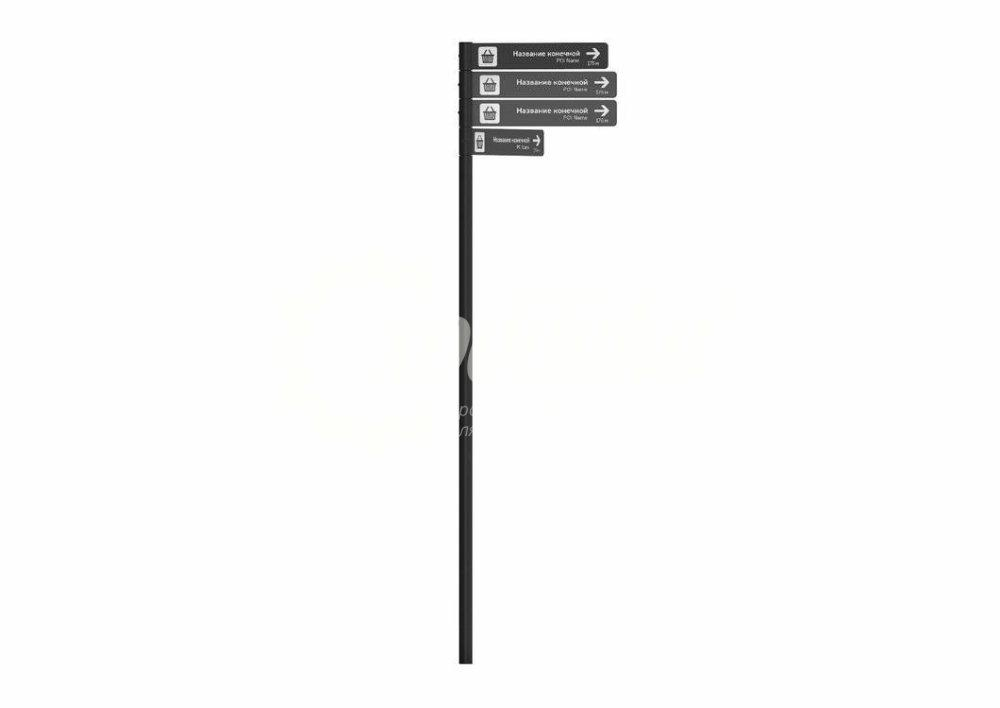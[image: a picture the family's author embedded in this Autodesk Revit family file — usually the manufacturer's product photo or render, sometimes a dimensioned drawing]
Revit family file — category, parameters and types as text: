
# Revit family: 11093 Указатель «Яуза» А 2.0 с табличками Хоббика
name_source: partatom
category: Антураж
revit_build: Autodesk Revit 2018 (Build: 20180423_1000(x64)
units: mm (PartAtom-declared; Revit-internal decimal feet)

## family parameters
Всегда вертикально = Да
Источник визуального образа = Геометрия семейства
На основе рабочей плоскости = Нет
Общий = Нет
При загрузке вырезать с полостями = Нет
Точка расчета площади = Нет

## types (2) — shared parameters
URL = https://hobbyka.ru
Артикул товара = Арт. 11093
Высота = 3290 мм
Группа модели = Стенды и указатели
Длина = 876 мм
Изготовитель = ООО «Хоббика»
Изображение типоразмера = Указатель «Яуза» А 2.0 с табличками Арт 11093.jpg
Материал изделия = Сталь
Ширина = 76 мм

## per-type parameters (varying)
| type | 4 таблички | 8 табличек | Описание | Число табличек |
| На 4 таблички | Да | Нет | Указатель «Яуза» А 2.0 с табличками. Версия на 4 таблички | 600 мм |
| На 8 табличек | Нет | Да | Указатель «Яуза» А 2.0 с табличками. Версия на 8 табличек | 1200 мм |
